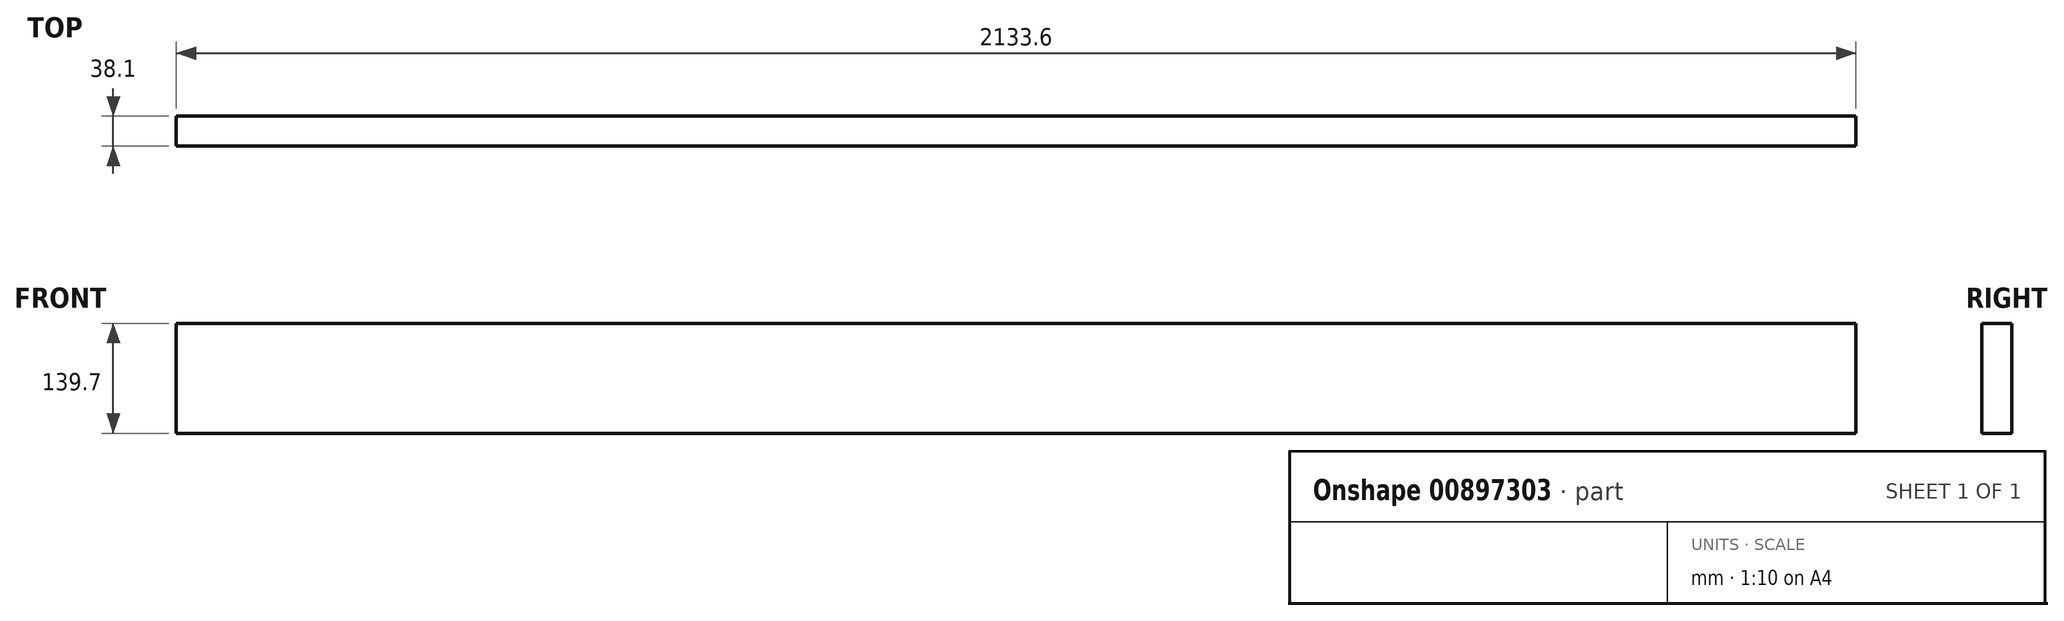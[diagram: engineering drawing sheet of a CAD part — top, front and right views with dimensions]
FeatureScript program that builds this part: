
annotation { "Feature Type Name" : "Feature", "Feature Type Description" : "" }
export const myFeature = defineFeature(function(context is Context, id is Id, definition is map)
    precondition{}
    {
        {
            var Q0;
            Q0=qCreatedBy(makeId("Right.planeOp"),FACE);
            var sketch = newSketch(context, id + "F0", { "sketchPlane" : qUnion([Q0])});
            skLineSegment(sketch, "E0.bottom", {"start": v(0.24, 93.76) * mm, "end": v(38.34, 93.76) * mm});
            skLineSegment(sketch, "E0.top", {"start": v(0.24, -45.94) * mm, "end": v(38.34, -45.94) * mm});
            skLineSegment(sketch, "E0.left", {"start": v(0.24, 93.76) * mm, "end": v(0.24, -45.94) * mm});
            skLineSegment(sketch, "E0.right", {"start": v(38.34, 93.76) * mm, "end": v(38.34, -45.94) * mm});
            skSolve(sketch);
        }
        {
            var Q0;
            Q0=makeQuery(id+"F0.imprint","IMPRINT",FACE,{"disambiguationData":[TD([[makeQuery(id+"F0.imprint","IMPRINT",EDGE,{"derivedFrom":sQuery(id+"F0.wireOp",EDGE,"E0.bottom")}),-1.0]])]});
            extrude(context, id + "F1", {"entities" : qUnion([Q0]), "depth" : 2133.6 * mm, "offsetDistance" : 25.4 * mm});
        }
    });
